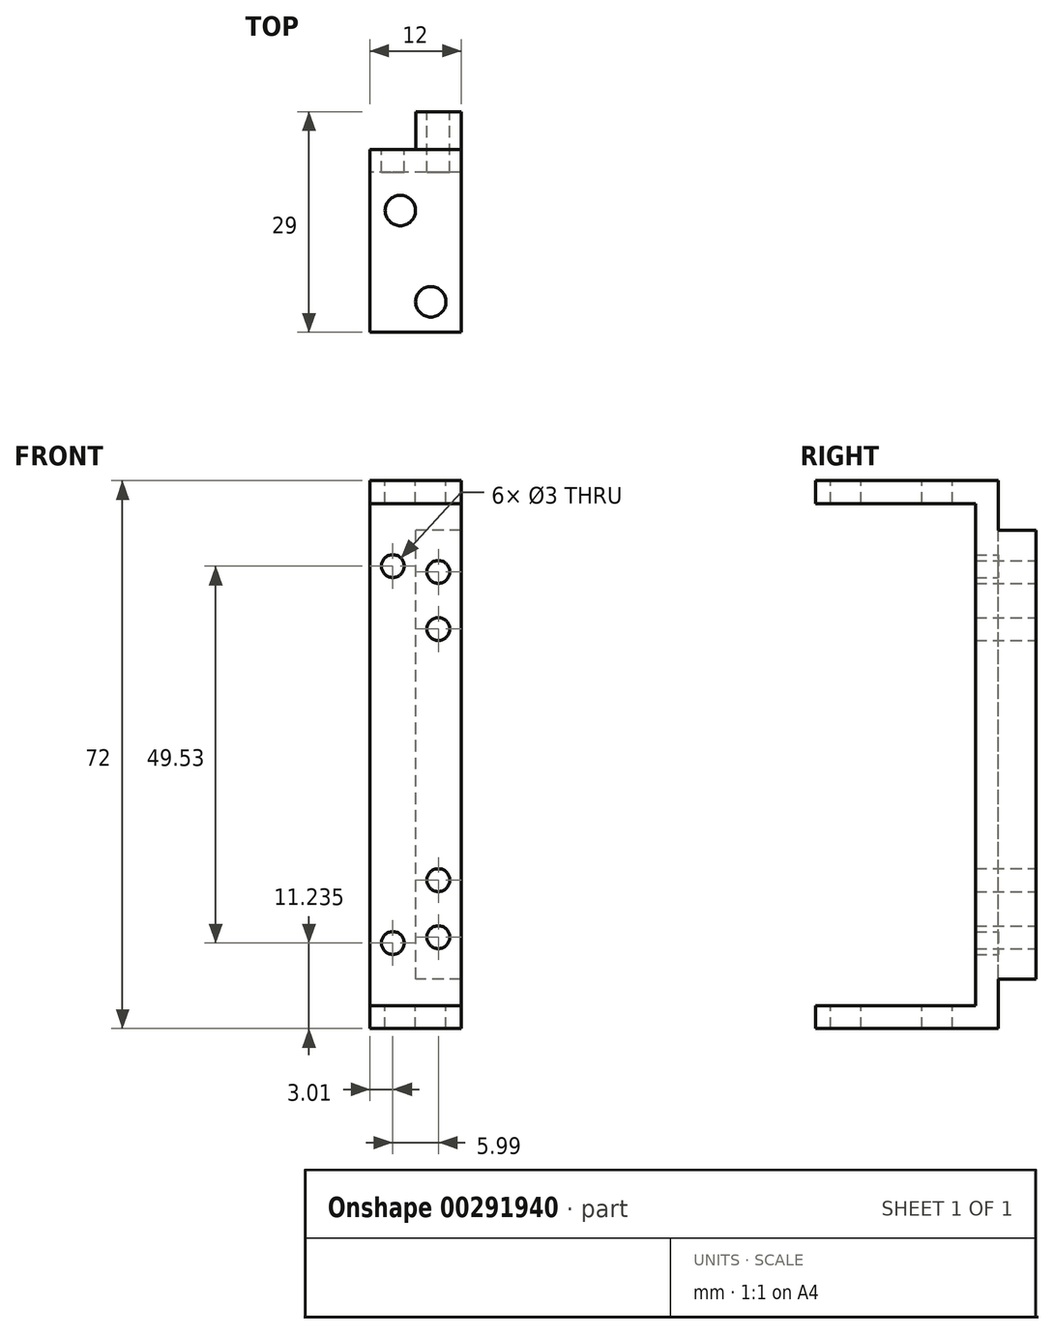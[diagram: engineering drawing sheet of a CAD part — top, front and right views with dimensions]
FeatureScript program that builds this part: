
annotation { "Feature Type Name" : "Feature", "Feature Type Description" : "" }
export const myFeature = defineFeature(function(context is Context, id is Id, definition is map)
    precondition{}
    {
        {
            var Q0;
            Q0=qCreatedBy(makeId("Right.planeOp"),FACE);
            var sketch = newSketch(context, id + "F0", { "sketchPlane" : qUnion([Q0])});
            skLineSegment(sketch, "E0", {"start": v(-10.5, 37.5) * mm, "end": v(18.5, 37.5) * mm});
            skLineSegment(sketch, "E1", {"start": v(18.5, 37.5) * mm, "end": v(18.5, -34.5) * mm});
            skLineSegment(sketch, "E2.0", {"start": v(10.5, 34.5) * mm, "end": v(10.5, -34.5) * mm});
            skLineSegment(sketch, "E2.1", {"start": v(-10.5, 34.5) * mm, "end": v(10.5, 34.5) * mm});
            skLineSegment(sketch, "E3", {"start": v(-10.5, 37.5) * mm, "end": v(-10.5, 34.5) * mm});
            skLineSegment(sketch, "E4", {"start": v(18.5, -34.5) * mm, "end": v(10.5, -34.5) * mm});
            skLineSegment(sketch, "E5", {"start": v(10.5, 0) * mm, "end": v(-14.36, 0) * mm, "construction": true});
            skLineSegment(sketch, "E6", {"start": v(0, 34.5) * mm, "end": v(0, -1.72) * mm, "construction": true});
            skSolve(sketch);
        }
        {
            var Q0;
            Q0=makeQuery(id+"F0.imprint","IMPRINT",FACE,{"disambiguationData":[TD([[makeQuery(id+"F0.imprint","IMPRINT",EDGE,{"derivedFrom":sQuery(id+"F0.wireOp",EDGE,"E0")}),-1.0]])]});
            extrude(context, id + "F1", {"entities" : qUnion([Q0]), "depth" : 12 * mm});
        }
        {
            var Q0;
            Q0=makeQuery(id+"F1.opExtrude","SWEPT_FACE",FACE,{"disambiguationData":[OSD([sQuery(id+"F0.wireOp",EDGE,"E0")])]});
            var sketch = newSketch(context, id + "F2", { "sketchPlane" : qUnion([Q0])});
            skLineSegment(sketch, "E7.bottom", {"start": v(0, 18.5) * mm, "end": v(6.02, 18.5) * mm});
            skLineSegment(sketch, "E7.top", {"start": v(0, 13.5) * mm, "end": v(6.02, 13.5) * mm});
            skLineSegment(sketch, "E7.left", {"start": v(0, 18.5) * mm, "end": v(0, 13.5) * mm});
            skLineSegment(sketch, "E7.right", {"start": v(6.02, 18.5) * mm, "end": v(6.02, 13.5) * mm});
            skSolve(sketch);
        }
        {
            var Q0;
            Q0=makeQuery(id+"F2.imprint","IMPRINT",FACE,{"disambiguationData":[TD([[makeQuery(id+"F2.imprint","IMPRINT",EDGE,{"derivedFrom":sQuery(id+"F2.wireOp",EDGE,"E7.bottom")}),1.0]])]});
            extrude(context, id + "F3", {"entities" : qUnion([Q0]), "operationType" : NewBodyOperationType.REMOVE, "oppositeDirection" : true, "depth" : 72 * mm});
        }
        {
            var Q0;
            Q0=makeQuery(id+"F1.opExtrude","SWEPT_FACE",FACE,{"disambiguationData":[OSD([sQuery(id+"F0.wireOp",EDGE,"E1")])]});
            var sketch = newSketch(context, id + "F4", { "sketchPlane" : qUnion([Q0])});
            skCircle(sketch, "E8", {"center": v(-9, 25.5) * mm, "radius": 1.5 * mm});
            skCircle(sketch, "E9", {"center": v(-9, -22.5) * mm, "radius": 1.5 * mm});
            skLineSegment(sketch, "E10", {"start": v(-9, 25.5) * mm, "end": v(-9, -22.5) * mm, "construction": true});
            skPoint(sketch, "E11", {"position": v(-9, 37.5) * mm});
            skLineSegment(sketch, "E12", {"start": v(-9, 25.5) * mm, "end": v(-9, 37.5) * mm, "construction": true});
            skSolve(sketch);
        }
        {
            var Q0;
            Q0=makeQuery(id+"F4.imprint","IMPRINT",FACE,{"disambiguationData":[TD([[makeQuery(id+"F4.imprint","IMPRINT",EDGE,{"derivedFrom":sQuery(id+"F4.wireOp",EDGE,"E8")}),1.0]])]});
            var Q1;
            Q1=makeQuery(id+"F4.imprint","IMPRINT",FACE,{"disambiguationData":[TD([[makeQuery(id+"F4.imprint","IMPRINT",EDGE,{"derivedFrom":sQuery(id+"F4.wireOp",EDGE,"E9")}),1.0]])]});
            extrude(context, id + "F5", {"entities" : qUnion([Q0, Q1]), "operationType" : NewBodyOperationType.REMOVE, "oppositeDirection" : true, "depth" : 25 * mm});
        }
        {
            var Q0;
            Q0=makeQuery(id+"F3.boolean.opBoolean","COPY",FACE,{"derivedFrom":makeQuery(id+"F3.opExtrude","SWEPT_FACE",FACE,{"disambiguationData":[OSD([sQuery(id+"F2.wireOp",EDGE,"E7.top")])]})});
            var sketch = newSketch(context, id + "F6", { "sketchPlane" : qUnion([Q0])});
            skCircle(sketch, "E13", {"center": v(-3, 26.27) * mm, "radius": 1.5 * mm});
            skCircle(sketch, "E14", {"center": v(-3, -23.27) * mm, "radius": 1.5 * mm});
            skLineSegment(sketch, "E15", {"start": v(-3, 26.27) * mm, "end": v(-3, -23.27) * mm, "construction": true});
            skPoint(sketch, "E16", {"position": v(-3, 37.5) * mm});
            skSolve(sketch);
        }
        {
            var Q0;
            Q0=makeQuery(id+"F6.imprint","IMPRINT",FACE,{"disambiguationData":[TD([[makeQuery(id+"F6.imprint","IMPRINT",EDGE,{"derivedFrom":sQuery(id+"F6.wireOp",EDGE,"E14")}),1.0]])]});
            var Q1;
            Q1=makeQuery(id+"F6.imprint","IMPRINT",FACE,{"disambiguationData":[TD([[makeQuery(id+"F6.imprint","IMPRINT",EDGE,{"derivedFrom":sQuery(id+"F6.wireOp",EDGE,"E13")}),1.0]])]});
            extrude(context, id + "F7", {"entities" : qUnion([Q0, Q1]), "operationType" : NewBodyOperationType.REMOVE, "oppositeDirection" : true, "depth" : 25 * mm});
        }
        {
            var Q0;
            Q0=makeQuery(id+"F1.opExtrude","SWEPT_FACE",FACE,{"disambiguationData":[OSD([sQuery(id+"F0.wireOp",EDGE,"E2.0")])]});
            var sketch = newSketch(context, id + "F8", { "sketchPlane" : qUnion([Q0])});
            skLineSegment(sketch, "E17.bottom", {"start": v(0, -34.5) * mm, "end": v(12, -34.5) * mm});
            skLineSegment(sketch, "E17.top", {"start": v(0, -31.5) * mm, "end": v(12, -31.5) * mm});
            skLineSegment(sketch, "E17.left", {"start": v(0, -31.5) * mm, "end": v(0, -34.5) * mm});
            skLineSegment(sketch, "E17.right", {"start": v(12, -31.5) * mm, "end": v(12, -34.5) * mm});
            skSolve(sketch);
        }
        {
            var Q0;
            Q0=makeQuery(id+"F8.imprint","IMPRINT",FACE,{"disambiguationData":[TD([[makeQuery(id+"F8.imprint","IMPRINT",EDGE,{"derivedFrom":sQuery(id+"F8.wireOp",EDGE,"E17.bottom")}),-1.0]])]});
            extrude(context, id + "F9", {"entities" : qUnion([Q0]), "operationType" : NewBodyOperationType.ADD, "depth" : 21 * mm});
        }
        {
            var Q0;
            Q0=makeQuery(id+"F1.opExtrude","SWEPT_FACE",FACE,{"disambiguationData":[OSD([sQuery(id+"F0.wireOp",EDGE,"E0")])]});
            var sketch = newSketch(context, id + "F10", { "sketchPlane" : qUnion([Q0])});
            skCircle(sketch, "E18", {"center": v(4, 5.5) * mm, "radius": 2 * mm});
            skCircle(sketch, "E19", {"center": v(8, -6.5) * mm, "radius": 2 * mm});
            skSolve(sketch);
        }
        {
            var Q0;
            Q0=makeQuery(id+"F10.imprint","IMPRINT",FACE,{"disambiguationData":[TD([[makeQuery(id+"F10.imprint","IMPRINT",EDGE,{"derivedFrom":sQuery(id+"F10.wireOp",EDGE,"E18")}),1.0]])]});
            var Q1;
            Q1=makeQuery(id+"F10.imprint","IMPRINT",FACE,{"disambiguationData":[TD([[makeQuery(id+"F10.imprint","IMPRINT",EDGE,{"derivedFrom":sQuery(id+"F10.wireOp",EDGE,"E19")}),1.0]])]});
            extrude(context, id + "F11", {"entities" : qUnion([Q0, Q1]), "operationType" : NewBodyOperationType.REMOVE, "oppositeDirection" : true, "depth" : 72 * mm});
        }
        {
            var Q0;
            Q0=makeQuery(id+"F1.opExtrude","SWEPT_FACE",FACE,{"disambiguationData":[OSD([sQuery(id+"F0.wireOp",EDGE,"E1")])]});
            var sketch = newSketch(context, id + "F12", { "sketchPlane" : qUnion([Q0])});
            skLineSegment(sketch, "E20.bottom", {"start": v(-12, 37.5) * mm, "end": v(-6.02, 37.5) * mm});
            skLineSegment(sketch, "E20.top", {"start": v(-12, 31) * mm, "end": v(-6.02, 31) * mm});
            skLineSegment(sketch, "E20.left", {"start": v(-12, 37.5) * mm, "end": v(-12, 31) * mm});
            skLineSegment(sketch, "E20.right", {"start": v(-6.02, 37.5) * mm, "end": v(-6.02, 31) * mm});
            skLineSegment(sketch, "E21.bottom", {"start": v(-12, -34.5) * mm, "end": v(-6.02, -34.5) * mm});
            skLineSegment(sketch, "E21.top", {"start": v(-12, -28) * mm, "end": v(-6.02, -28) * mm});
            skLineSegment(sketch, "E21.left", {"start": v(-12, -34.5) * mm, "end": v(-12, -28) * mm});
            skLineSegment(sketch, "E21.right", {"start": v(-6.02, -34.5) * mm, "end": v(-6.02, -28) * mm});
            skSolve(sketch);
        }
        {
            var Q0;
            Q0=qSketchRegion(id+"F12",true);
            extrude(context, id + "F13", {"entities" : qUnion([Q0]), "operationType" : NewBodyOperationType.REMOVE, "oppositeDirection" : true, "depth" : 5 * mm});
        }
        {
            var Q0;
            Q0=makeQuery(id+"F1.opExtrude","SWEPT_FACE",FACE,{"disambiguationData":[OSD([sQuery(id+"F0.wireOp",EDGE,"E1")])]});
            var sketch = newSketch(context, id + "F14", { "sketchPlane" : qUnion([Q0])});
            skCircle(sketch, "E22", {"center": v(-9, -15) * mm, "radius": 1.5 * mm});
            skCircle(sketch, "E23", {"center": v(-9, 18) * mm, "radius": 1.5 * mm});
            skLineSegment(sketch, "E24", {"start": v(-9, 18) * mm, "end": v(-9, -15) * mm, "construction": true});
            skSolve(sketch);
        }
        {
            var Q0;
            Q0=qSketchRegion(id+"F14",true);
            extrude(context, id + "F15", {"entities" : qUnion([Q0]), "operationType" : NewBodyOperationType.REMOVE, "oppositeDirection" : true, "depth" : 25 * mm});
        }
    });
